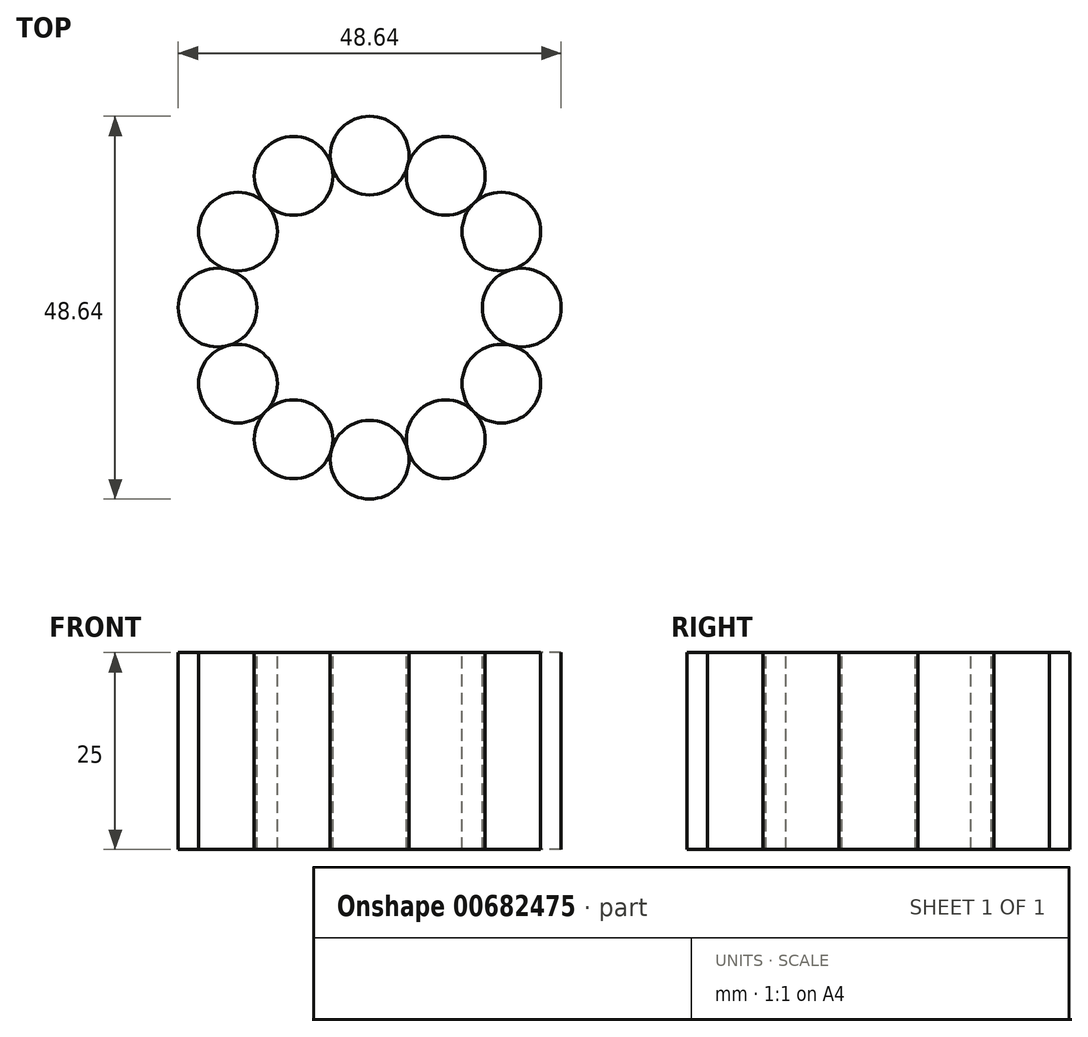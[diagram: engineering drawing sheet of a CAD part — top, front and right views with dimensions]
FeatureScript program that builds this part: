
annotation { "Feature Type Name" : "Feature", "Feature Type Description" : "" }
export const myFeature = defineFeature(function(context is Context, id is Id, definition is map)
    precondition{}
    {
        {
            var Q0;
            Q0=qCreatedBy(makeId("Top.planeOp"),FACE);
            var sketch = newSketch(context, id + "F0", { "sketchPlane" : qUnion([Q0])});
            skCircle(sketch, "E0", {"center": v(0, 0) * mm, "radius": 14.32 * mm});
            skCircle(sketch, "E1", {"center": v(0, 19.32) * mm, "radius": 5 * mm});
            skCircle(sketch, "E2.1.0", {"center": v(-9.66, 16.73) * mm, "radius": 5 * mm});
            skCircle(sketch, "E2.2.0", {"center": v(-16.73, 9.66) * mm, "radius": 5 * mm});
            skCircle(sketch, "E2.3.0", {"center": v(-19.32, 0) * mm, "radius": 5 * mm});
            skCircle(sketch, "E2.4.0", {"center": v(-16.73, -9.66) * mm, "radius": 5 * mm});
            skCircle(sketch, "E2.5.0", {"center": v(-9.66, -16.73) * mm, "radius": 5 * mm});
            skCircle(sketch, "E2.6.0", {"center": v(0, -19.32) * mm, "radius": 5 * mm});
            skCircle(sketch, "E2.7.0", {"center": v(9.66, -16.73) * mm, "radius": 5 * mm});
            skCircle(sketch, "E3.1.8.0", {"center": v(16.73, -9.66) * mm, "radius": 5 * mm});
            skCircle(sketch, "E3.1.9.0", {"center": v(19.32, 0) * mm, "radius": 5 * mm});
            skCircle(sketch, "E4.1.10.0", {"center": v(16.73, 9.66) * mm, "radius": 5 * mm});
            skCircle(sketch, "E4.1.11.0", {"center": v(9.66, 16.73) * mm, "radius": 5 * mm});
            skSolve(sketch);
        }
        {
            var Q0;
            {var subQ0=sQuery(id+"F0.wireOp",EDGE,"E2.1.0");var subQ1=makeQuery(id+"F0.imprint","INTERSECT",VERTEX,{"derivedFrom":[subQ0,sQuery(id+"F0.wireOp",EDGE,"E2.2.0")]});Q0=makeQuery(id+"F0.imprint","IMPRINT",FACE,{"disambiguationData":[TD([[makeQuery(id+"F0.imprint","IMPRINT",EDGE,{"disambiguationData":[TD([[subQ1,-1.0]])],"derivedFrom":subQ0}),1.0]])]});}
            var Q1;
            {var subQ0=sQuery(id+"F0.wireOp",EDGE,"E1");var subQ1=makeQuery(id+"F0.imprint","INTERSECT",VERTEX,{"derivedFrom":[subQ0,sQuery(id+"F0.wireOp",EDGE,"E2.1.0")]});Q1=makeQuery(id+"F0.imprint","IMPRINT",FACE,{"disambiguationData":[TD([[makeQuery(id+"F0.imprint","IMPRINT",EDGE,{"disambiguationData":[TD([[subQ1,-1.0]])],"derivedFrom":subQ0}),1.0]])]});}
            var Q2;
            {var subQ0=sQuery(id+"F0.wireOp",EDGE,"E4.1.11.0");var subQ1=makeQuery(id+"F0.imprint","INTERSECT",VERTEX,{"derivedFrom":[sQuery(id+"F0.wireOp",EDGE,"E1"),subQ0]});Q2=makeQuery(id+"F0.imprint","IMPRINT",FACE,{"disambiguationData":[TD([[makeQuery(id+"F0.imprint","IMPRINT",EDGE,{"disambiguationData":[TD([[subQ1,-1.0]])],"derivedFrom":subQ0}),1.0]])]});}
            var Q3;
            {var subQ0=sQuery(id+"F0.wireOp",EDGE,"E4.1.10.0");var subQ1=makeQuery(id+"F0.imprint","INTERSECT",VERTEX,{"derivedFrom":[subQ0,sQuery(id+"F0.wireOp",EDGE,"E4.1.11.0")]});Q3=makeQuery(id+"F0.imprint","IMPRINT",FACE,{"disambiguationData":[TD([[makeQuery(id+"F0.imprint","IMPRINT",EDGE,{"disambiguationData":[TD([[subQ1,-1.0]])],"derivedFrom":subQ0}),1.0]])]});}
            var Q4;
            {var subQ0=sQuery(id+"F0.wireOp",EDGE,"E3.1.9.0");var subQ1=makeQuery(id+"F0.imprint","INTERSECT",VERTEX,{"derivedFrom":[subQ0,sQuery(id+"F0.wireOp",EDGE,"E4.1.10.0")]});Q4=makeQuery(id+"F0.imprint","IMPRINT",FACE,{"disambiguationData":[TD([[makeQuery(id+"F0.imprint","IMPRINT",EDGE,{"disambiguationData":[TD([[subQ1,-1.0]])],"derivedFrom":subQ0}),1.0]])]});}
            var Q5;
            {var subQ0=sQuery(id+"F0.wireOp",EDGE,"E3.1.8.0");var subQ1=makeQuery(id+"F0.imprint","INTERSECT",VERTEX,{"derivedFrom":[subQ0,sQuery(id+"F0.wireOp",EDGE,"E3.1.9.0")]});Q5=makeQuery(id+"F0.imprint","IMPRINT",FACE,{"disambiguationData":[TD([[makeQuery(id+"F0.imprint","IMPRINT",EDGE,{"disambiguationData":[TD([[subQ1,-1.0]])],"derivedFrom":subQ0}),1.0]])]});}
            var Q6;
            {var subQ0=sQuery(id+"F0.wireOp",EDGE,"E2.7.0");var subQ1=makeQuery(id+"F0.imprint","INTERSECT",VERTEX,{"derivedFrom":[subQ0,sQuery(id+"F0.wireOp",EDGE,"E3.1.8.0")]});Q6=makeQuery(id+"F0.imprint","IMPRINT",FACE,{"disambiguationData":[TD([[makeQuery(id+"F0.imprint","IMPRINT",EDGE,{"disambiguationData":[TD([[subQ1,-1.0]])],"derivedFrom":subQ0}),1.0]])]});}
            var Q7;
            {var subQ0=sQuery(id+"F0.wireOp",EDGE,"E2.6.0");var subQ1=makeQuery(id+"F0.imprint","INTERSECT",VERTEX,{"derivedFrom":[subQ0,sQuery(id+"F0.wireOp",EDGE,"E2.7.0")]});Q7=makeQuery(id+"F0.imprint","IMPRINT",FACE,{"disambiguationData":[TD([[makeQuery(id+"F0.imprint","IMPRINT",EDGE,{"disambiguationData":[TD([[subQ1,-1.0]])],"derivedFrom":subQ0}),1.0]])]});}
            var Q8;
            {var subQ0=sQuery(id+"F0.wireOp",EDGE,"E2.5.0");var subQ1=makeQuery(id+"F0.imprint","INTERSECT",VERTEX,{"derivedFrom":[subQ0,sQuery(id+"F0.wireOp",EDGE,"E2.6.0")]});Q8=makeQuery(id+"F0.imprint","IMPRINT",FACE,{"disambiguationData":[TD([[makeQuery(id+"F0.imprint","IMPRINT",EDGE,{"disambiguationData":[TD([[subQ1,-1.0]])],"derivedFrom":subQ0}),1.0]])]});}
            var Q9;
            {var subQ0=sQuery(id+"F0.wireOp",EDGE,"E2.4.0");var subQ1=makeQuery(id+"F0.imprint","INTERSECT",VERTEX,{"derivedFrom":[subQ0,sQuery(id+"F0.wireOp",EDGE,"E2.5.0")]});Q9=makeQuery(id+"F0.imprint","IMPRINT",FACE,{"disambiguationData":[TD([[makeQuery(id+"F0.imprint","IMPRINT",EDGE,{"disambiguationData":[TD([[subQ1,-1.0]])],"derivedFrom":subQ0}),1.0]])]});}
            var Q10;
            {var subQ0=sQuery(id+"F0.wireOp",EDGE,"E2.3.0");var subQ1=makeQuery(id+"F0.imprint","INTERSECT",VERTEX,{"derivedFrom":[subQ0,sQuery(id+"F0.wireOp",EDGE,"E2.4.0")]});Q10=makeQuery(id+"F0.imprint","IMPRINT",FACE,{"disambiguationData":[TD([[makeQuery(id+"F0.imprint","IMPRINT",EDGE,{"disambiguationData":[TD([[subQ1,-1.0]])],"derivedFrom":subQ0}),1.0]])]});}
            var Q11;
            {var subQ0=sQuery(id+"F0.wireOp",EDGE,"E2.2.0");var subQ1=makeQuery(id+"F0.imprint","INTERSECT",VERTEX,{"derivedFrom":[subQ0,sQuery(id+"F0.wireOp",EDGE,"E2.3.0")]});Q11=makeQuery(id+"F0.imprint","IMPRINT",FACE,{"disambiguationData":[TD([[makeQuery(id+"F0.imprint","IMPRINT",EDGE,{"disambiguationData":[TD([[subQ1,-1.0]])],"derivedFrom":subQ0}),1.0]])]});}
            extrude(context, id + "F1", {"entities" : qUnion([Q0, Q1, Q2, Q3, Q4, Q5, Q6, Q7, Q8, Q9, Q10, Q11]), "oppositeDirection" : true, "depth" : 25 * mm, "offsetDistance" : 25 * mm});
        }
    });
